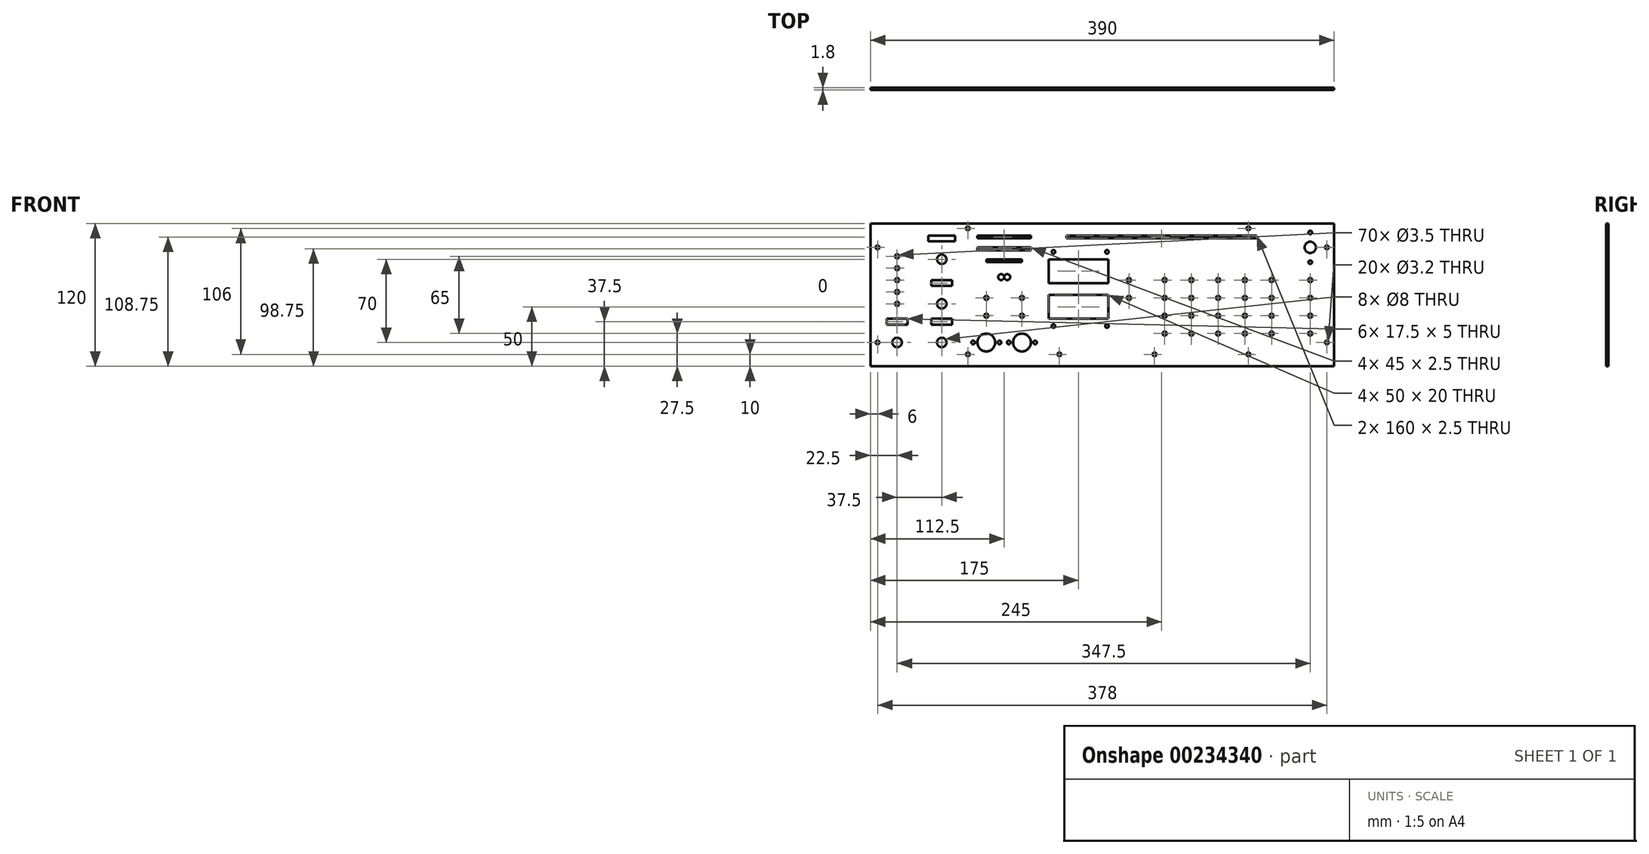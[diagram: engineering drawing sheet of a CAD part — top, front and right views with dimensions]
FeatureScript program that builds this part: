
annotation { "Feature Type Name" : "Feature", "Feature Type Description" : "" }
export const myFeature = defineFeature(function(context is Context, id is Id, definition is map)
    precondition{}
    {
        {
            var Q0;
            Q0=qCreatedBy(makeId("Front.planeOp"),FACE);
            var sketch = newSketch(context, id + "F0", { "sketchPlane" : qUnion([Q0])});
            skLineSegment(sketch, "E0.bottom", {"start": v(195, -60) * mm, "end": v(-195, -60) * mm});
            skLineSegment(sketch, "E0.top", {"start": v(195, 60) * mm, "end": v(-195, 60) * mm});
            skLineSegment(sketch, "E0.left", {"start": v(195, -60) * mm, "end": v(195, 60) * mm});
            skLineSegment(sketch, "E0.right", {"start": v(-195, -60) * mm, "end": v(-195, 60) * mm});
            skPoint(sketch, "E0.middle", {"position": v(0, 0) * mm});
            skLineSegment(sketch, "E1.bottom", {"start": v(-45, 30) * mm, "end": v(5, 30) * mm});
            skLineSegment(sketch, "E1.top", {"start": v(-45, 10) * mm, "end": v(5, 10) * mm});
            skLineSegment(sketch, "E1.left", {"start": v(-45, 30) * mm, "end": v(-45, 10) * mm});
            skLineSegment(sketch, "E1.right", {"start": v(5, 30) * mm, "end": v(5, 10) * mm});
            skLineSegment(sketch, "E2", {"start": v(-45, 60) * mm, "end": v(-45, -60) * mm, "construction": true});
            skLineSegment(sketch, "E3.bottom", {"start": v(-45, 0) * mm, "end": v(5, 0) * mm});
            skLineSegment(sketch, "E3.top", {"start": v(-45, -20) * mm, "end": v(5, -20) * mm});
            skLineSegment(sketch, "E3.left", {"start": v(-45, 0) * mm, "end": v(-45, -20) * mm});
            skLineSegment(sketch, "E3.right", {"start": v(5, 0) * mm, "end": v(5, -20) * mm});
            skLineSegment(sketch, "E4", {"start": v(-172.5, 60) * mm, "end": v(-172.5, -60) * mm, "construction": true});
            skCircle(sketch, "E5", {"center": v(-172.5, 32.5) * mm, "radius": 1.75 * mm});
            skCircle(sketch, "E6.0.1.0", {"center": v(-172.5, 22.5) * mm, "radius": 1.75 * mm});
            skCircle(sketch, "E6.0.2.0", {"center": v(-172.5, 12.5) * mm, "radius": 1.75 * mm});
            skCircle(sketch, "E6.0.3.0", {"center": v(-172.5, 2.5) * mm, "radius": 1.75 * mm});
            skCircle(sketch, "E6.0.4.0", {"center": v(-172.5, -7.5) * mm, "radius": 1.75 * mm});
            skLineSegment(sketch, "E6.direction2", {"start": v(-172.5, 32.5) * mm, "end": v(-172.5, 22.5) * mm, "construction": true});
            skCircle(sketch, "E7", {"center": v(-172.5, -40) * mm, "radius": 4 * mm});
            skCircle(sketch, "E8", {"center": v(-135, 30) * mm, "radius": 4 * mm});
            skCircle(sketch, "E9", {"center": v(-135, -40) * mm, "radius": 4 * mm});
            skCircle(sketch, "E10", {"center": v(-135, -7.5) * mm, "radius": 4 * mm});
            skLineSegment(sketch, "E11.bottom", {"start": v(130, 47.5) * mm, "end": v(-30, 47.5) * mm});
            skLineSegment(sketch, "E11.top", {"start": v(130, 50) * mm, "end": v(-30, 50) * mm});
            skLineSegment(sketch, "E11.left", {"start": v(130, 47.5) * mm, "end": v(130, 50) * mm});
            skLineSegment(sketch, "E11.right", {"start": v(-30, 47.5) * mm, "end": v(-30, 50) * mm});
            skPoint(sketch, "E11.middle", {"position": v(50, 48.75) * mm});
            skLineSegment(sketch, "E12", {"start": v(-30, 50) * mm, "end": v(-195, 50) * mm, "construction": true});
            skLineSegment(sketch, "E13.bottom", {"start": v(-123.75, 50) * mm, "end": v(-146.25, 50) * mm});
            skLineSegment(sketch, "E13.top", {"start": v(-123.75, 45) * mm, "end": v(-146.25, 45) * mm});
            skLineSegment(sketch, "E13.left", {"start": v(-123.75, 50) * mm, "end": v(-123.75, 45) * mm});
            skLineSegment(sketch, "E13.right", {"start": v(-146.25, 50) * mm, "end": v(-146.25, 45) * mm});
            skPoint(sketch, "E13.middle", {"position": v(-135, 47.5) * mm});
            skCircle(sketch, "E14", {"center": v(-97.5, -40) * mm, "radius": 7.5 * mm});
            skCircle(sketch, "E15", {"center": v(-67.5, -40) * mm, "radius": 7.5 * mm});
            skLineSegment(sketch, "E16", {"start": v(-97.5, 30) * mm, "end": v(-97.5, -60) * mm, "construction": true});
            skLineSegment(sketch, "E17", {"start": v(-67.5, 30) * mm, "end": v(-67.5, -60) * mm, "construction": true});
            skLineSegment(sketch, "E18.bottom", {"start": v(-60, 50) * mm, "end": v(-105, 50) * mm});
            skLineSegment(sketch, "E18.top", {"start": v(-60, 47.5) * mm, "end": v(-105, 47.5) * mm});
            skLineSegment(sketch, "E18.left", {"start": v(-60, 50) * mm, "end": v(-60, 47.5) * mm});
            skLineSegment(sketch, "E18.right", {"start": v(-105, 50) * mm, "end": v(-105, 47.5) * mm});
            skPoint(sketch, "E18.middle", {"position": v(-82.5, 48.75) * mm});
            skPoint(sketch, "E18.middle.positionSnap0", {"position": v(-82.5, 30) * mm});
            skLineSegment(sketch, "E19.bottom", {"start": v(-60, 40) * mm, "end": v(-105, 40) * mm});
            skLineSegment(sketch, "E19.top", {"start": v(-60, 37.5) * mm, "end": v(-105, 37.5) * mm});
            skLineSegment(sketch, "E19.left", {"start": v(-60, 40) * mm, "end": v(-60, 37.5) * mm});
            skLineSegment(sketch, "E19.right", {"start": v(-105, 40) * mm, "end": v(-105, 37.5) * mm});
            skPoint(sketch, "E19.middle", {"position": v(-82.5, 38.75) * mm});
            skLineSegment(sketch, "E20.bottom", {"start": v(-97.5, 27.5) * mm, "end": v(-67.5, 27.5) * mm});
            skLineSegment(sketch, "E20.top", {"start": v(-97.5, 30) * mm, "end": v(-67.5, 30) * mm});
            skLineSegment(sketch, "E20.left", {"start": v(-97.5, 27.5) * mm, "end": v(-97.5, 30) * mm});
            skLineSegment(sketch, "E20.right", {"start": v(-67.5, 27.5) * mm, "end": v(-67.5, 30) * mm});
            skPoint(sketch, "E20.middle", {"position": v(-82.5, 28.75) * mm});
            skCircle(sketch, "E21", {"center": v(175, 40) * mm, "radius": 4.75 * mm});
            skCircle(sketch, "E22", {"center": v(-97.5, -2.5) * mm, "radius": 1.75 * mm});
            skCircle(sketch, "E23", {"center": v(-67.5, -2.5) * mm, "radius": 1.75 * mm});
            skCircle(sketch, "E24", {"center": v(-67.5, -17.5) * mm, "radius": 1.75 * mm});
            skCircle(sketch, "E25", {"center": v(-97.5, -17.5) * mm, "radius": 1.75 * mm});
            skCircle(sketch, "E26", {"center": v(22.5, 12.5) * mm, "radius": 1.75 * mm});
            skCircle(sketch, "E27", {"center": v(22.5, -2.5) * mm, "radius": 1.75 * mm});
            skCircle(sketch, "E28", {"center": v(52.5, 12.5) * mm, "radius": 1.75 * mm});
            skCircle(sketch, "E29.0.1.0", {"center": v(52.5, -2.5) * mm, "radius": 1.75 * mm});
            skCircle(sketch, "E29.0.2.0", {"center": v(52.5, -17.5) * mm, "radius": 1.75 * mm});
            skCircle(sketch, "E29.0.3.0", {"center": v(52.5, -32.5) * mm, "radius": 1.75 * mm});
            skCircle(sketch, "E29.1.0.0", {"center": v(75, 12.5) * mm, "radius": 1.75 * mm});
            skCircle(sketch, "E29.1.1.0", {"center": v(75, -2.5) * mm, "radius": 1.75 * mm});
            skCircle(sketch, "E29.1.2.0", {"center": v(75, -17.5) * mm, "radius": 1.75 * mm});
            skCircle(sketch, "E29.1.3.0", {"center": v(75, -32.5) * mm, "radius": 1.75 * mm});
            skCircle(sketch, "E29.2.0.0", {"center": v(97.5, 12.5) * mm, "radius": 1.75 * mm});
            skCircle(sketch, "E29.2.1.0", {"center": v(97.5, -2.5) * mm, "radius": 1.75 * mm});
            skCircle(sketch, "E29.2.2.0", {"center": v(97.5, -17.5) * mm, "radius": 1.75 * mm});
            skCircle(sketch, "E29.2.3.0", {"center": v(97.5, -32.5) * mm, "radius": 1.75 * mm});
            skCircle(sketch, "E29.3.0.0", {"center": v(120, 12.5) * mm, "radius": 1.75 * mm});
            skCircle(sketch, "E29.3.1.0", {"center": v(120, -2.5) * mm, "radius": 1.75 * mm});
            skCircle(sketch, "E29.3.2.0", {"center": v(120, -17.5) * mm, "radius": 1.75 * mm});
            skCircle(sketch, "E29.3.3.0", {"center": v(120, -32.5) * mm, "radius": 1.75 * mm});
            skCircle(sketch, "E29.4.0.0", {"center": v(142.5, 12.5) * mm, "radius": 1.75 * mm});
            skCircle(sketch, "E29.4.1.0", {"center": v(142.5, -2.5) * mm, "radius": 1.75 * mm});
            skCircle(sketch, "E29.4.2.0", {"center": v(142.5, -17.5) * mm, "radius": 1.75 * mm});
            skCircle(sketch, "E29.4.3.0", {"center": v(142.5, -32.5) * mm, "radius": 1.75 * mm});
            skLineSegment(sketch, "E29.direction1", {"start": v(52.5, 12.5) * mm, "end": v(75, 12.5) * mm, "construction": true});
            skLineSegment(sketch, "E29.direction2", {"start": v(52.5, 12.5) * mm, "end": v(52.5, -2.5) * mm, "construction": true});
            skCircle(sketch, "E30", {"center": v(-85, 15) * mm, "radius": 2.5 * mm});
            skCircle(sketch, "E31", {"center": v(-79.9, 15) * mm, "radius": 2.5 * mm});
            skLineSegment(sketch, "E32.bottom", {"start": v(-163.75, -25) * mm, "end": v(-181.25, -25) * mm});
            skLineSegment(sketch, "E32.top", {"start": v(-163.75, -20) * mm, "end": v(-181.25, -20) * mm});
            skLineSegment(sketch, "E32.left", {"start": v(-163.75, -25) * mm, "end": v(-163.75, -20) * mm});
            skLineSegment(sketch, "E32.right", {"start": v(-181.25, -25) * mm, "end": v(-181.25, -20) * mm});
            skPoint(sketch, "E32.middle", {"position": v(-172.5, -22.5) * mm});
            skLineSegment(sketch, "E33.bottom", {"start": v(-126.25, -25) * mm, "end": v(-143.75, -25) * mm});
            skLineSegment(sketch, "E33.top", {"start": v(-126.25, -20) * mm, "end": v(-143.75, -20) * mm});
            skLineSegment(sketch, "E33.left", {"start": v(-126.25, -25) * mm, "end": v(-126.25, -20) * mm});
            skLineSegment(sketch, "E33.right", {"start": v(-143.75, -25) * mm, "end": v(-143.75, -20) * mm});
            skPoint(sketch, "E33.middle", {"position": v(-135, -22.5) * mm});
            skCircle(sketch, "E34", {"center": v(175, 12.5) * mm, "radius": 1.75 * mm});
            skCircle(sketch, "E35.0.1.0", {"center": v(175, -2.5) * mm, "radius": 1.75 * mm});
            skCircle(sketch, "E35.0.2.0", {"center": v(175, -17.5) * mm, "radius": 1.75 * mm});
            skCircle(sketch, "E35.0.3.0", {"center": v(175, -32.5) * mm, "radius": 1.75 * mm});
            skLineSegment(sketch, "E35.direction1", {"start": v(175, 12.5) * mm, "end": v(185.3, 12.5) * mm, "construction": true});
            skLineSegment(sketch, "E35.direction2", {"start": v(175, 12.5) * mm, "end": v(175, -2.5) * mm, "construction": true});
            skLineSegment(sketch, "E36.bottom", {"start": v(-126.25, 7.5) * mm, "end": v(-143.75, 7.5) * mm});
            skLineSegment(sketch, "E36.top", {"start": v(-126.25, 12.5) * mm, "end": v(-143.75, 12.5) * mm});
            skLineSegment(sketch, "E36.left", {"start": v(-126.25, 7.5) * mm, "end": v(-126.25, 12.5) * mm});
            skLineSegment(sketch, "E36.right", {"start": v(-143.75, 7.5) * mm, "end": v(-143.75, 12.5) * mm});
            skPoint(sketch, "E36.middle", {"position": v(-135, 10) * mm});
            skCircle(sketch, "E37", {"center": v(-189, 40) * mm, "radius": 1.6 * mm});
            skCircle(sketch, "E38", {"center": v(-189, -40) * mm, "radius": 1.6 * mm});
            skCircle(sketch, "E39", {"center": v(-113, -50) * mm, "radius": 1.6 * mm});
            skCircle(sketch, "E40", {"center": v(-36, -50) * mm, "radius": 1.6 * mm});
            skCircle(sketch, "E41", {"center": v(123, -50) * mm, "radius": 1.6 * mm});
            skCircle(sketch, "E42", {"center": v(189, -40) * mm, "radius": 1.6 * mm});
            skCircle(sketch, "E43", {"center": v(189, 40) * mm, "radius": 1.6 * mm});
            skLineSegment(sketch, "E44", {"start": v(-195, -40) * mm, "end": v(-45, -40) * mm, "construction": true});
            skCircle(sketch, "E45", {"center": v(-108.6, -40) * mm, "radius": 1.5 * mm});
            skCircle(sketch, "E46", {"center": v(-78.6, -40) * mm, "radius": 1.5 * mm});
            skCircle(sketch, "E47.MirrorC", {"center": v(-86.4, -40) * mm, "radius": 1.5 * mm});
            skCircle(sketch, "E48.MirrorC", {"center": v(-56.4, -40) * mm, "radius": 1.5 * mm});
            skCircle(sketch, "E49", {"center": v(44, -50) * mm, "radius": 1.6 * mm});
            skCircle(sketch, "E50", {"center": v(175, 52.5) * mm, "radius": 1.5 * mm});
            skLineSegment(sketch, "E51", {"start": v(175, 40) * mm, "end": v(195, 40) * mm, "construction": true});
            skCircle(sketch, "E52.MirrorC", {"center": v(175, 27.5) * mm, "radius": 1.5 * mm});
            skCircle(sketch, "E53", {"center": v(-41, 36.25) * mm, "radius": 1.5 * mm});
            skCircle(sketch, "E54", {"center": v(-41, -26.25) * mm, "radius": 1.5 * mm});
            skCircle(sketch, "E55", {"center": v(4, -26.25) * mm, "radius": 1.5 * mm});
            skCircle(sketch, "E56", {"center": v(4, 36.25) * mm, "radius": 1.5 * mm});
            skCircle(sketch, "E57", {"center": v(-113, 56) * mm, "radius": 1.6 * mm});
            skCircle(sketch, "E58", {"center": v(123, 56) * mm, "radius": 1.6 * mm});
            skSolve(sketch);
        }
        {
            var Q0;
            Q0=makeQuery(id+"F0.imprint","IMPRINT",FACE,{"disambiguationData":[TD([[makeQuery(id+"F0.imprint","IMPRINT",EDGE,{"derivedFrom":sQuery(id+"F0.wireOp",EDGE,"E0.bottom")}),-1.0]])]});
            extrude(context, id + "F1", {"entities" : qUnion([Q0]), "depth" : 1.8 * mm});
        }
    });
